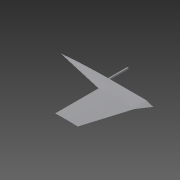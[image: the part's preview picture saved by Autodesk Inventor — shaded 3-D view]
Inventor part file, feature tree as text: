
AUTODESK INVENTOR PART (.ipt)
format: ipt  version: 2014 SP1 (Build 180222100, 222)  size: 186,368 bytes
history: native  units: mm
features: sketch x4, plane x3, loft x2, fillet x1, extrude x1, other x1
ambient origin geometry x8: Origin, YZ Plane, XZ Plane, XY Plane, X Axis, Y Axis, Z Axis, Center Point
bodies: Solid1 (feature_tree)
feature tree (12):
  sketch  "Sketch1"  dims[d0=490.0mm d11=60.0mm]
  plane  "Work Plane1"
  sketch  "Sketch2"  dims[d12=230.0mm d13=120.0mm d14=0.0mm d15=90.0deg]
  plane  "Work Plane2"
  loft  "Loft1"
  loft  "Loft2"
  plane  "Work Plane3"
  fillet  "Fillet1"  [1 undecoded]
  extrude  "Extrusion3"  TaperAngle=0.0deg  [1 undecoded]
  sketch  "Sketch3"  dims[d16=0.0mm d17=90.0deg d18=0.0mm d19=90.0deg]
  other  "Edges1"
  sketch  "Sketch5"  dims[d20=0.0mm d21=90.0deg d22=0.0mm d30=40.0mm d31=10.0mm d32=110.0mm d33=0.0mm]
note: 2 required parameter values undecoded (feature->parameter linkage not recoverable at this tier; creation-order binding heuristic only, values carry confidence <= 0.55)
